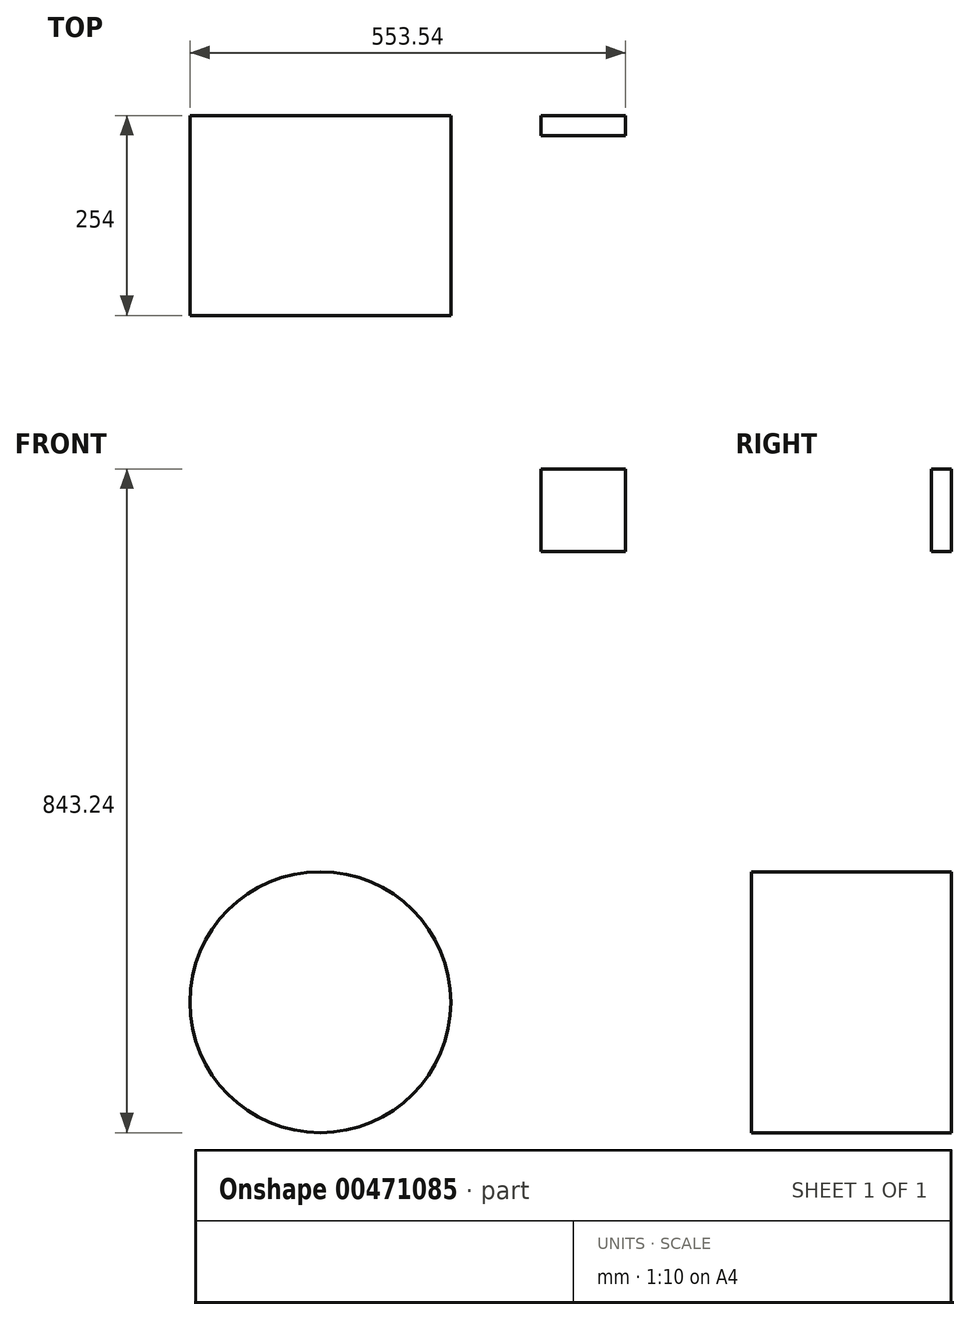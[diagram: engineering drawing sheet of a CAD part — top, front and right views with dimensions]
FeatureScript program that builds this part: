
annotation { "Feature Type Name" : "Feature", "Feature Type Description" : "" }
export const myFeature = defineFeature(function(context is Context, id is Id, definition is map)
    precondition{}
    {
        {
            var Q0;
            Q0=qCreatedBy(makeId("Front.planeOp"),FACE);
            var sketch = newSketch(context, id + "F0", { "sketchPlane" : qUnion([Q0])});
            skLineSegment(sketch, "E0.bottom", {"start": v(53.84, 52.34) * mm, "end": v(-53.84, 52.34) * mm});
            skLineSegment(sketch, "E0.top", {"start": v(53.84, -52.34) * mm, "end": v(-53.84, -52.34) * mm});
            skLineSegment(sketch, "E0.left", {"start": v(53.84, 52.34) * mm, "end": v(53.84, -52.34) * mm});
            skLineSegment(sketch, "E0.right", {"start": v(-53.84, 52.34) * mm, "end": v(-53.84, -52.34) * mm});
            skPoint(sketch, "E0.middle", {"position": v(0, 0) * mm});
            skSolve(sketch);
        }
        {
            var Q0;
            Q0=makeQuery(id+"F0.imprint","IMPRINT",FACE,{"disambiguationData":[TD([[makeQuery(id+"F0.imprint","IMPRINT",EDGE,{"derivedFrom":sQuery(id+"F0.wireOp",EDGE,"E0.bottom")}),1.0]])]});
            var sketch = newSketch(context, id + "F1", { "sketchPlane" : qUnion([Q0])});
            skSolve(sketch);
        }
        {
            var Q0;
            Q0=makeQuery(id+"F1.imprint","IMPRINT",FACE,{"disambiguationData":[TD([[makeQuery(id+"F1.imprint","IMPRINT",EDGE,{"derivedFrom":makeQuery(id+"F0.imprint","IMPRINT",EDGE,{"derivedFrom":sQuery(id+"F0.wireOp",EDGE,"E0.bottom")})}),1.0]])]});
            extrude(context, id + "F2", {"entities" : qUnion([Q0]), "depth" : 25.4 * mm});
        }
        {
            var Q0;
            Q0 = qSketchRegion(id + "F0", true);
            var sketch = newSketch(context, id + "F3", { "sketchPlane" : qUnion([Q0])});
            skCircle(sketch, "E1", {"center": v(-333.93, -625.13) * mm, "radius": 165.77 * mm});
            skPoint(sketch, "E1.first.point", {"position": v(-174, -581.54) * mm});
            skPoint(sketch, "E1.second.point", {"position": v(-168.18, -627.44) * mm});
            skPoint(sketch, "E1.third.point", {"position": v(-185.84, -699.6) * mm});
            skSolve(sketch);
        }
        {
            var Q0;
            Q0=makeQuery(id+"F3.imprint","IMPRINT",FACE,{"disambiguationData":[TD([[makeQuery(id+"F3.imprint","IMPRINT",EDGE,{"derivedFrom":sQuery(id+"F3.wireOp",EDGE,"E1")}),1.0]])]});
            extrude(context, id + "F4", {"entities" : qUnion([Q0]), "depth" : 254 * mm});
        }
    });
